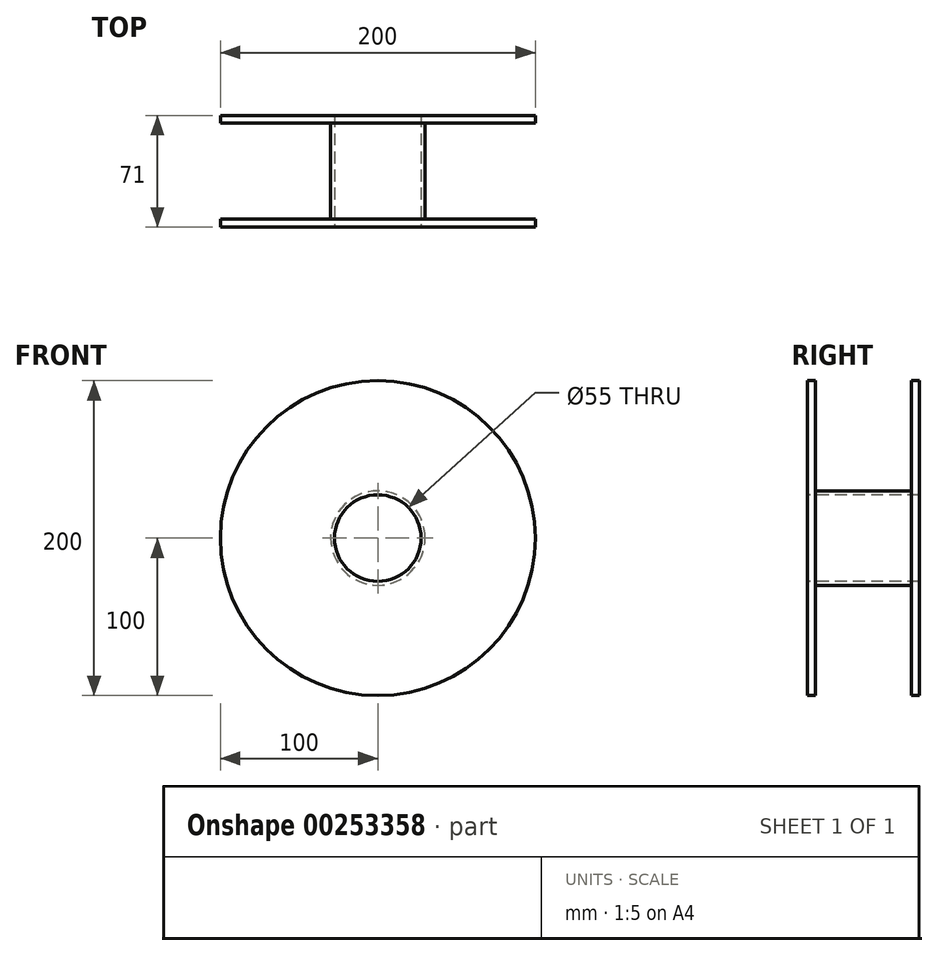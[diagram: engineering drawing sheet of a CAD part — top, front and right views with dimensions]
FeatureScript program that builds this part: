
annotation { "Feature Type Name" : "Feature", "Feature Type Description" : "" }
export const myFeature = defineFeature(function(context is Context, id is Id, definition is map)
    precondition{}
    {
        {
            var Q0;
            Q0=qCreatedBy(makeId("Front.planeOp"),FACE);
            var sketch = newSketch(context, id + "F0", { "sketchPlane" : qUnion([Q0])});
            skCircle(sketch, "E0", {"center": v(0, 0) * mm, "radius": 100 * mm});
            skCircle(sketch, "E1", {"center": v(0, 0) * mm, "radius": 30 * mm});
            skCircle(sketch, "E2", {"center": v(0, 0) * mm, "radius": 27.5 * mm});
            skSolve(sketch);
        }
        {
            var Q0;
            Q0 = qSketchRegion(id + "F0", true);
            extrude(context, id + "F1", {"entities" : qUnion([Q0]), "oppositeDirection" : true, "depth" : 5 * mm});
        }
        {
            var Q0;
            Q0=makeQuery(id+"F1.opExtrude","CAP_FACE",FACE,{"disambiguationData":[OSD([sQuery(id+"F0.wireOp",EDGE,"E0"),sQuery(id+"F0.wireOp",EDGE,"E1")])],"isStart":false});
            extrude(context, id + "F2", {"entities" : qUnion([Q0]), "depth" : 66 * mm, "hasSecondDirection" : true, "secondDirectionOppositeDirection" : false, "secondDirectionDepth" : 61 * mm});
        }
        {
            var Q0;
            Q0=makeQuery(id+"F0.imprint","IMPRINT",FACE,{"disambiguationData":[TD([[makeQuery(id+"F0.imprint","IMPRINT",EDGE,{"derivedFrom":sQuery(id+"F0.wireOp",EDGE,"E1")}),1.0]])]});
            extrude(context, id + "F3", {"entities" : qUnion([Q0]), "operationType" : NewBodyOperationType.ADD, "oppositeDirection" : true, "depth" : 71 * mm});
        }
    });
